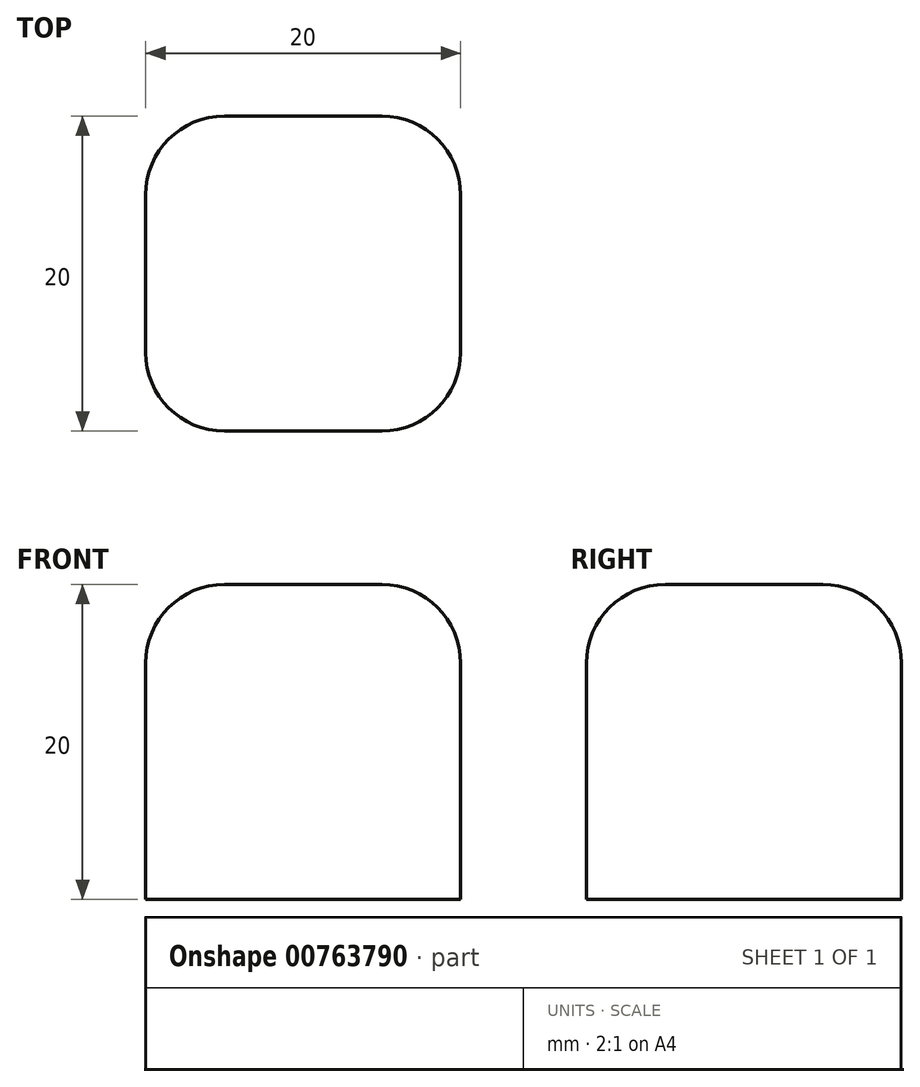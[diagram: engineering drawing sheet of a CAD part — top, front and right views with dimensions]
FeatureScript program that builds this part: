
annotation { "Feature Type Name" : "Feature", "Feature Type Description" : "" }
export const myFeature = defineFeature(function(context is Context, id is Id, definition is map)
    precondition{}
    {
        {
            var Q0;
            Q0=qCreatedBy(makeId("Front.planeOp"),FACE);
            var sketch = newSketch(context, id + "F0", { "sketchPlane" : qUnion([Q0])});
            skLineSegment(sketch, "E0.bottom", {"start": v(0, 0) * mm, "end": v(20, 0) * mm});
            skLineSegment(sketch, "E0.top", {"start": v(0, 20) * mm, "end": v(20, 20) * mm});
            skLineSegment(sketch, "E0.left", {"start": v(0, 0) * mm, "end": v(0, 20) * mm});
            skLineSegment(sketch, "E0.right", {"start": v(20, 0) * mm, "end": v(20, 20) * mm});
            skSolve(sketch);
        }
        {
            var Q0;
            Q0 = qSketchRegion(id + "F0", true);
            extrude(context, id + "F1", {"entities" : qUnion([Q0]), "depth" : 20 * mm, "offsetDistance" : 25 * mm});
        }
        {
            var Q0;
            Q0=makeQuery(id+"F1.opExtrude","CAP_EDGE",EDGE,{"disambiguationData":[OSD([sQuery(id+"F0.wireOp",EDGE,"E0.top")])],"isStart":true});
            var Q1;
            Q1=makeQuery(id+"F1.opExtrude","SWEPT_EDGE",EDGE,{"disambiguationData":[OSD([sQuery(id+"F0.wireOp",EDGE,"E0.top"),sQuery(id+"F0.wireOp",EDGE,"E0.right")])]});
            var Q2;
            Q2=makeQuery(id+"F1.opExtrude","CAP_EDGE",EDGE,{"disambiguationData":[OSD([sQuery(id+"F0.wireOp",EDGE,"E0.top")])],"isStart":false});
            var Q3;
            Q3=makeQuery(id+"F1.opExtrude","SWEPT_EDGE",EDGE,{"disambiguationData":[OSD([sQuery(id+"F0.wireOp",EDGE,"E0.top"),sQuery(id+"F0.wireOp",EDGE,"E0.left")])]});
            var Q4;
            Q4=makeQuery(id+"F1.opExtrude","CAP_EDGE",EDGE,{"disambiguationData":[OSD([sQuery(id+"F0.wireOp",EDGE,"E0.right")])],"isStart":false});
            var Q5;
            Q5=makeQuery(id+"F1.opExtrude","CAP_EDGE",EDGE,{"disambiguationData":[OSD([sQuery(id+"F0.wireOp",EDGE,"E0.right")])],"isStart":true});
            var Q6;
            Q6=makeQuery(id+"F1.opExtrude","CAP_EDGE",EDGE,{"disambiguationData":[OSD([sQuery(id+"F0.wireOp",EDGE,"E0.left")])],"isStart":true});
            var Q7;
            Q7=makeQuery(id+"F1.opExtrude","CAP_EDGE",EDGE,{"disambiguationData":[OSD([sQuery(id+"F0.wireOp",EDGE,"E0.left")])],"isStart":false});
            fillet(context, id + "F2", {"entities" : qUnion([Q0, Q1, Q2, Q3, Q4, Q5, Q6, Q7]), "radius" : 5 * mm, "tangentPropagation" : true, "allowEdgeOverflow" : false});
        }
    });
